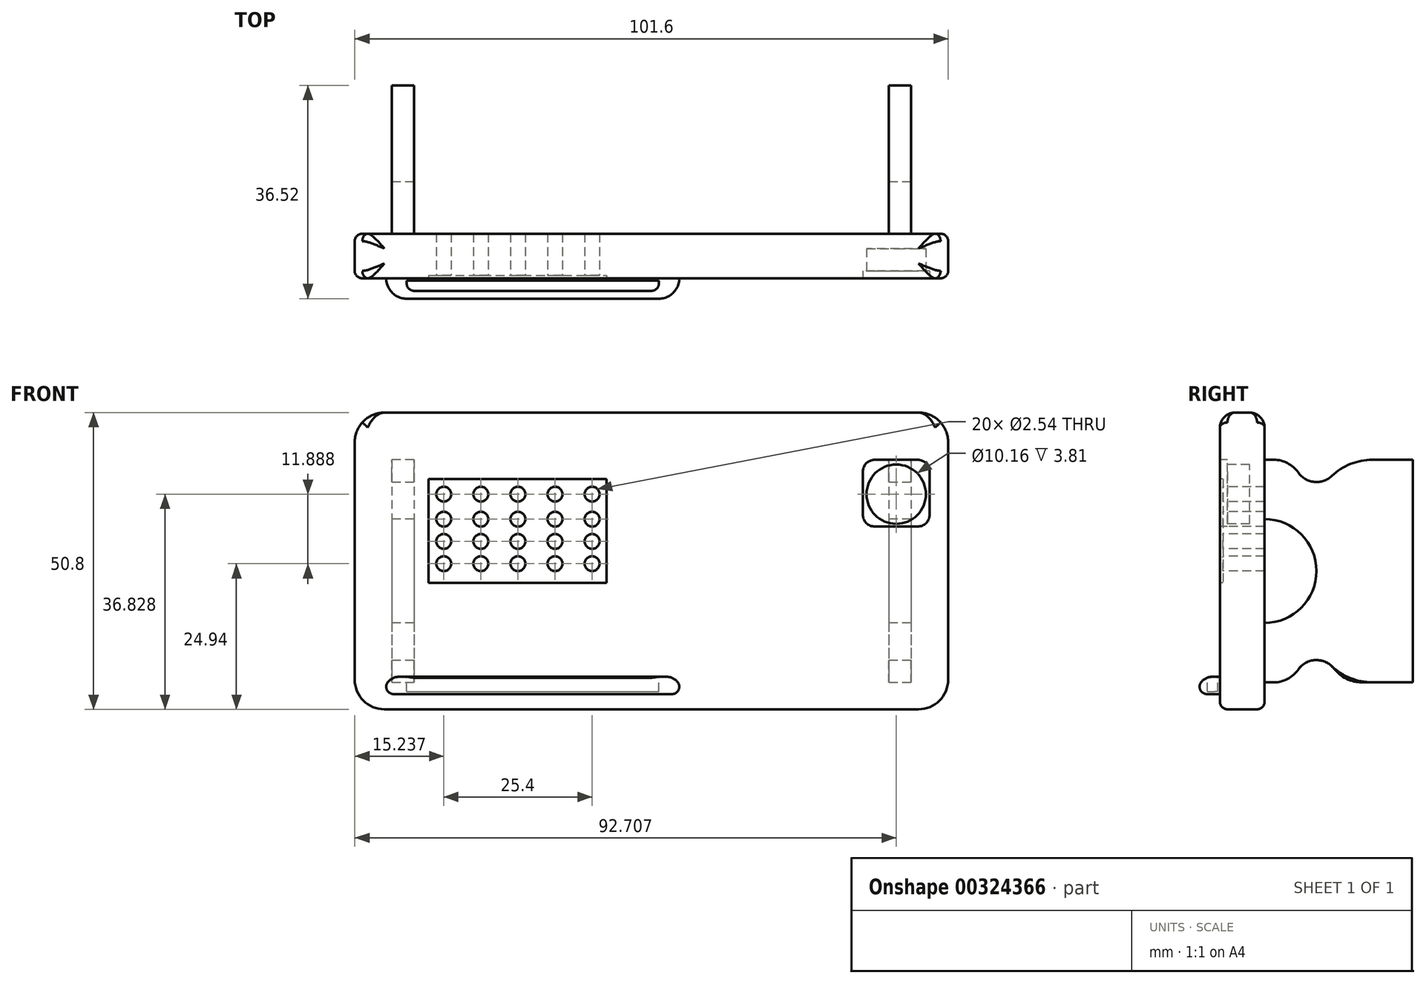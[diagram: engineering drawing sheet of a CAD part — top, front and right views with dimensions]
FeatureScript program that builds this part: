
annotation { "Feature Type Name" : "Feature", "Feature Type Description" : "" }
export const myFeature = defineFeature(function(context is Context, id is Id, definition is map)
    precondition{}
    {
        {
            var Q0;
            Q0=qCreatedBy(makeId("Front.planeOp"),FACE);
            var sketch = newSketch(context, id + "F0", { "sketchPlane" : qUnion([Q0])});
            skLineSegment(sketch, "E0.bottom", {"start": v(-68.61, 8.08) * mm, "end": v(32.99, 8.08) * mm});
            skLineSegment(sketch, "E0.top", {"start": v(-68.61, -42.72) * mm, "end": v(32.99, -42.72) * mm});
            skLineSegment(sketch, "E0.left", {"start": v(-68.61, 8.08) * mm, "end": v(-68.61, -42.72) * mm});
            skLineSegment(sketch, "E0.right", {"start": v(32.99, 8.08) * mm, "end": v(32.99, -42.72) * mm});
            skSolve(sketch);
        }
        {
            var Q0;
            Q0=makeQuery(id+"F0.imprint","IMPRINT",FACE,{"disambiguationData":[TD([[makeQuery(id+"F0.imprint","IMPRINT",EDGE,{"derivedFrom":sQuery(id+"F0.wireOp",EDGE,"E0.bottom")}),-1.0]])]});
            extrude(context, id + "F1", {"entities" : qUnion([Q0]), "depth" : 7.62 * mm});
        }
        {
            var Q0;
            Q0=makeQuery(id+"F1.opExtrude","SWEPT_EDGE",EDGE,{"disambiguationData":[OSD([sQuery(id+"F0.wireOp",EDGE,"E0.bottom"),sQuery(id+"F0.wireOp",EDGE,"E0.left")])]});
            var Q1;
            Q1=makeQuery(id+"F1.opExtrude","SWEPT_EDGE",EDGE,{"disambiguationData":[OSD([sQuery(id+"F0.wireOp",EDGE,"E0.bottom"),sQuery(id+"F0.wireOp",EDGE,"E0.right")])]});
            fillet(context, id + "F2", {"entities" : qUnion([Q0, Q1]), "radius" : 5.08 * mm, "tangentPropagation" : true, "allowEdgeOverflow" : false});
        }
        {
            var Q0;
            Q0=makeQuery(id+"F1.opExtrude","CAP_FACE",FACE,{"disambiguationData":[OSD([sQuery(id+"F0.wireOp",EDGE,"E0.bottom"),sQuery(id+"F0.wireOp",EDGE,"E0.top"),sQuery(id+"F0.wireOp",EDGE,"E0.left"),sQuery(id+"F0.wireOp",EDGE,"E0.right")])],"isStart":false});
            var sketch = newSketch(context, id + "F3", { "sketchPlane" : qUnion([Q0])});
            skLineSegment(sketch, "E1.bottom", {"start": v(-63.53, -37.14) * mm, "end": v(-12.73, -37.14) * mm});
            skLineSegment(sketch, "E1.top", {"start": v(-63.53, -40.12) * mm, "end": v(-12.73, -40.12) * mm});
            skLineSegment(sketch, "E1.left", {"start": v(-63.53, -37.14) * mm, "end": v(-63.53, -40.12) * mm});
            skLineSegment(sketch, "E1.right", {"start": v(-12.73, -37.14) * mm, "end": v(-12.73, -40.12) * mm});
            skSolve(sketch);
        }
        {
            var Q0;
            Q0=makeQuery(id+"F1.opExtrude","SWEPT_EDGE",EDGE,{"disambiguationData":[OSD([sQuery(id+"F0.wireOp",EDGE,"E0.top"),sQuery(id+"F0.wireOp",EDGE,"E0.right")])]});
            var Q1;
            Q1=makeQuery(id+"F1.opExtrude","SWEPT_EDGE",EDGE,{"disambiguationData":[OSD([sQuery(id+"F0.wireOp",EDGE,"E0.top"),sQuery(id+"F0.wireOp",EDGE,"E0.left")])]});
            fillet(context, id + "F4", {"entities" : qUnion([Q0, Q1]), "radius" : 5.08 * mm, "tangentPropagation" : true, "allowEdgeOverflow" : false});
        }
        {
            var Q0;
            Q0=makeQuery(id+"F1.opExtrude","CAP_FACE",FACE,{"disambiguationData":[OSD([sQuery(id+"F0.wireOp",EDGE,"E0.bottom"),sQuery(id+"F0.wireOp",EDGE,"E0.top"),sQuery(id+"F0.wireOp",EDGE,"E0.left"),sQuery(id+"F0.wireOp",EDGE,"E0.right")])],"isStart":false});
            var sketch = newSketch(context, id + "F5", { "sketchPlane" : qUnion([Q0])});
            skLineSegment(sketch, "E2.bottom", {"start": v(19.02, -0.81) * mm, "end": v(29.18, -0.81) * mm});
            skLineSegment(sketch, "E2.top", {"start": v(19.02, -10.97) * mm, "end": v(29.18, -10.97) * mm});
            skLineSegment(sketch, "E2.left", {"start": v(19.02, -0.81) * mm, "end": v(19.02, -10.97) * mm});
            skLineSegment(sketch, "E2.right", {"start": v(29.18, -0.81) * mm, "end": v(29.18, -10.97) * mm});
            skSolve(sketch);
        }
        {
            var Q0;
            Q0=makeQuery(id+"F5.imprint","IMPRINT",FACE,{"disambiguationData":[TD([[makeQuery(id+"F5.imprint","IMPRINT",EDGE,{"derivedFrom":sQuery(id+"F5.wireOp",EDGE,"E2.bottom")}),-1.0]])]});
            extrude(context, id + "F6", {"entities" : qUnion([Q0]), "operationType" : NewBodyOperationType.REMOVE, "oppositeDirection" : true, "depth" : 5.08 * mm});
        }
        {
            var Q0;
            Q0=makeQuery(id+"F6.boolean.opBoolean","COPY",EDGE,{"derivedFrom":makeQuery(id+"F6.opExtrude","SWEPT_EDGE",EDGE,{"disambiguationData":[OSD([sQuery(id+"F5.wireOp",EDGE,"E2.bottom"),sQuery(id+"F5.wireOp",EDGE,"E2.left")])]})});
            var Q1;
            Q1=makeQuery(id+"F6.boolean.opBoolean","COPY",EDGE,{"derivedFrom":makeQuery(id+"F6.opExtrude","SWEPT_EDGE",EDGE,{"disambiguationData":[OSD([sQuery(id+"F5.wireOp",EDGE,"E2.bottom"),sQuery(id+"F5.wireOp",EDGE,"E2.right")])]})});
            var Q2;
            Q2=makeQuery(id+"F6.boolean.opBoolean","COPY",EDGE,{"derivedFrom":makeQuery(id+"F6.opExtrude","SWEPT_EDGE",EDGE,{"disambiguationData":[OSD([sQuery(id+"F5.wireOp",EDGE,"E2.top"),sQuery(id+"F5.wireOp",EDGE,"E2.left")])]})});
            var Q3;
            Q3=makeQuery(id+"F6.boolean.opBoolean","COPY",EDGE,{"derivedFrom":makeQuery(id+"F6.opExtrude","SWEPT_EDGE",EDGE,{"disambiguationData":[OSD([sQuery(id+"F5.wireOp",EDGE,"E2.top"),sQuery(id+"F5.wireOp",EDGE,"E2.right")])]})});
            fillet(context, id + "F7", {"entities" : qUnion([Q0, Q1, Q2, Q3]), "radius" : 5.08 * mm, "tangentPropagation" : true, "allowEdgeOverflow" : false});
        }
        {
            var Q0;
            Q0=makeQuery(id+"F1.opExtrude","CAP_FACE",FACE,{"disambiguationData":[OSD([sQuery(id+"F0.wireOp",EDGE,"E0.bottom"),sQuery(id+"F0.wireOp",EDGE,"E0.top"),sQuery(id+"F0.wireOp",EDGE,"E0.left"),sQuery(id+"F0.wireOp",EDGE,"E0.right")])],"isStart":false});
            var sketch = newSketch(context, id + "F8", { "sketchPlane" : qUnion([Q0])});
            skLineSegment(sketch, "E3.bottom", {"start": v(18.38, 0) * mm, "end": v(29.8, 0) * mm});
            skLineSegment(sketch, "E3.top", {"start": v(18.38, -11.43) * mm, "end": v(29.8, -11.43) * mm});
            skLineSegment(sketch, "E3.left", {"start": v(18.38, 0) * mm, "end": v(18.38, -11.43) * mm});
            skLineSegment(sketch, "E3.right", {"start": v(29.8, 0) * mm, "end": v(29.8, -11.43) * mm});
            skSolve(sketch);
        }
        {
            var Q0;
            Q0=makeQuery(id+"F8.imprint","IMPRINT",FACE,{"disambiguationData":[TD([[makeQuery(id+"F8.imprint","IMPRINT",EDGE,{"derivedFrom":sQuery(id+"F8.wireOp",EDGE,"E3.bottom")}),-1.0]])]});
            extrude(context, id + "F9", {"entities" : qUnion([Q0]), "operationType" : NewBodyOperationType.REMOVE, "oppositeDirection" : true, "depth" : 1.27 * mm});
        }
        {
            var Q0;
            Q0=makeQuery(id+"F9.boolean.opBoolean","COPY",EDGE,{"derivedFrom":makeQuery(id+"F9.opExtrude","SWEPT_EDGE",EDGE,{"disambiguationData":[OSD([sQuery(id+"F8.wireOp",EDGE,"E3.top"),sQuery(id+"F8.wireOp",EDGE,"E3.right")])]})});
            var Q1;
            Q1=makeQuery(id+"F9.boolean.opBoolean","COPY",EDGE,{"derivedFrom":makeQuery(id+"F9.opExtrude","SWEPT_EDGE",EDGE,{"disambiguationData":[OSD([sQuery(id+"F8.wireOp",EDGE,"E3.top"),sQuery(id+"F8.wireOp",EDGE,"E3.left")])]})});
            var Q2;
            Q2=makeQuery(id+"F9.boolean.opBoolean","COPY",EDGE,{"derivedFrom":makeQuery(id+"F9.opExtrude","SWEPT_EDGE",EDGE,{"disambiguationData":[OSD([sQuery(id+"F8.wireOp",EDGE,"E3.bottom"),sQuery(id+"F8.wireOp",EDGE,"E3.left")])]})});
            var Q3;
            Q3=makeQuery(id+"F9.boolean.opBoolean","COPY",EDGE,{"derivedFrom":makeQuery(id+"F9.opExtrude","SWEPT_EDGE",EDGE,{"disambiguationData":[OSD([sQuery(id+"F8.wireOp",EDGE,"E3.bottom"),sQuery(id+"F8.wireOp",EDGE,"E3.right")])]})});
            fillet(context, id + "F10", {"entities" : qUnion([Q0, Q1, Q2, Q3]), "radius" : 2.03 * mm, "tangentPropagation" : true, "allowEdgeOverflow" : false});
        }
        {
            var Q0;
            Q0=makeQuery(id+"F1.opExtrude","SWEPT_FACE",FACE,{"disambiguationData":[OSD([sQuery(id+"F0.wireOp",EDGE,"E0.bottom")])]});
            fillet(context, id + "F11", {"entities" : qUnion([Q0]), "radius" : 2.54 * mm, "allowEdgeOverflow" : false});
        }
        {
            var Q0;
            Q0=makeQuery(id+"F1.opExtrude","CAP_FACE",FACE,{"disambiguationData":[OSD([sQuery(id+"F0.wireOp",EDGE,"E0.bottom"),sQuery(id+"F0.wireOp",EDGE,"E0.top"),sQuery(id+"F0.wireOp",EDGE,"E0.left"),sQuery(id+"F0.wireOp",EDGE,"E0.right")])],"isStart":false});
            var sketch = newSketch(context, id + "F12", { "sketchPlane" : qUnion([Q0])});
            skCircle(sketch, "E4", {"center": v(-53.37, -5.9) * mm, "radius": 1.27 * mm});
            skCircle(sketch, "E5", {"center": v(-53.37, -10.16) * mm, "radius": 1.27 * mm});
            skCircle(sketch, "E6", {"center": v(-53.37, -13.97) * mm, "radius": 1.27 * mm});
            skCircle(sketch, "E7", {"center": v(-53.37, -17.78) * mm, "radius": 1.27 * mm});
            skCircle(sketch, "E8", {"center": v(-47.02, -5.9) * mm, "radius": 1.27 * mm});
            skCircle(sketch, "E9", {"center": v(-47.02, -10.16) * mm, "radius": 1.27 * mm});
            skCircle(sketch, "E10", {"center": v(-47.02, -13.97) * mm, "radius": 1.27 * mm});
            skCircle(sketch, "E11", {"center": v(-47.02, -17.78) * mm, "radius": 1.27 * mm});
            skCircle(sketch, "E12", {"center": v(-40.67, -10.16) * mm, "radius": 1.27 * mm});
            skCircle(sketch, "E13", {"center": v(-40.67, -13.97) * mm, "radius": 1.27 * mm});
            skCircle(sketch, "E14", {"center": v(-40.67, -17.78) * mm, "radius": 1.27 * mm});
            skCircle(sketch, "E15", {"center": v(-40.67, -5.9) * mm, "radius": 1.27 * mm});
            skCircle(sketch, "E16", {"center": v(-34.32, -5.9) * mm, "radius": 1.27 * mm});
            skCircle(sketch, "E17", {"center": v(-34.32, -10.16) * mm, "radius": 1.27 * mm});
            skCircle(sketch, "E18", {"center": v(-34.32, -13.97) * mm, "radius": 1.27 * mm});
            skCircle(sketch, "E19", {"center": v(-34.32, -17.78) * mm, "radius": 1.27 * mm});
            skCircle(sketch, "E20", {"center": v(-27.97, -5.9) * mm, "radius": 1.27 * mm});
            skCircle(sketch, "E21", {"center": v(-27.97, -10.16) * mm, "radius": 1.27 * mm});
            skCircle(sketch, "E22", {"center": v(-27.97, -13.97) * mm, "radius": 1.27 * mm});
            skCircle(sketch, "E23", {"center": v(-27.97, -17.78) * mm, "radius": 1.27 * mm});
            skSolve(sketch);
        }
        {
            var Q0;
            Q0=makeQuery(id+"F12.imprint","IMPRINT",FACE,{"disambiguationData":[TD([[makeQuery(id+"F12.imprint","IMPRINT",EDGE,{"derivedFrom":sQuery(id+"F12.wireOp",EDGE,"E4")}),1.0]])]});
            var Q1;
            Q1=makeQuery(id+"F12.imprint","IMPRINT",FACE,{"disambiguationData":[TD([[makeQuery(id+"F12.imprint","IMPRINT",EDGE,{"derivedFrom":sQuery(id+"F12.wireOp",EDGE,"E5")}),1.0]])]});
            var Q2;
            Q2=makeQuery(id+"F12.imprint","IMPRINT",FACE,{"disambiguationData":[TD([[makeQuery(id+"F12.imprint","IMPRINT",EDGE,{"derivedFrom":sQuery(id+"F12.wireOp",EDGE,"E6")}),1.0]])]});
            var Q3;
            Q3=makeQuery(id+"F12.imprint","IMPRINT",FACE,{"disambiguationData":[TD([[makeQuery(id+"F12.imprint","IMPRINT",EDGE,{"derivedFrom":sQuery(id+"F12.wireOp",EDGE,"E7")}),1.0]])]});
            var Q4;
            Q4=makeQuery(id+"F12.imprint","IMPRINT",FACE,{"disambiguationData":[TD([[makeQuery(id+"F12.imprint","IMPRINT",EDGE,{"derivedFrom":sQuery(id+"F12.wireOp",EDGE,"E11")}),1.0]])]});
            var Q5;
            Q5=makeQuery(id+"F12.imprint","IMPRINT",FACE,{"disambiguationData":[TD([[makeQuery(id+"F12.imprint","IMPRINT",EDGE,{"derivedFrom":sQuery(id+"F12.wireOp",EDGE,"E10")}),1.0]])]});
            var Q6;
            Q6=makeQuery(id+"F12.imprint","IMPRINT",FACE,{"disambiguationData":[TD([[makeQuery(id+"F12.imprint","IMPRINT",EDGE,{"derivedFrom":sQuery(id+"F12.wireOp",EDGE,"E9")}),1.0]])]});
            var Q7;
            Q7=makeQuery(id+"F12.imprint","IMPRINT",FACE,{"disambiguationData":[TD([[makeQuery(id+"F12.imprint","IMPRINT",EDGE,{"derivedFrom":sQuery(id+"F12.wireOp",EDGE,"E8")}),1.0]])]});
            var Q8;
            Q8=makeQuery(id+"F12.imprint","IMPRINT",FACE,{"disambiguationData":[TD([[makeQuery(id+"F12.imprint","IMPRINT",EDGE,{"derivedFrom":sQuery(id+"F12.wireOp",EDGE,"E15")}),1.0]])]});
            var Q9;
            Q9=makeQuery(id+"F12.imprint","IMPRINT",FACE,{"disambiguationData":[TD([[makeQuery(id+"F12.imprint","IMPRINT",EDGE,{"derivedFrom":sQuery(id+"F12.wireOp",EDGE,"E16")}),1.0]])]});
            var Q10;
            Q10=makeQuery(id+"F12.imprint","IMPRINT",FACE,{"disambiguationData":[TD([[makeQuery(id+"F12.imprint","IMPRINT",EDGE,{"derivedFrom":sQuery(id+"F12.wireOp",EDGE,"E20")}),1.0]])]});
            var Q11;
            Q11=makeQuery(id+"F12.imprint","IMPRINT",FACE,{"disambiguationData":[TD([[makeQuery(id+"F12.imprint","IMPRINT",EDGE,{"derivedFrom":sQuery(id+"F12.wireOp",EDGE,"E12")}),1.0]])]});
            var Q12;
            Q12=makeQuery(id+"F12.imprint","IMPRINT",FACE,{"disambiguationData":[TD([[makeQuery(id+"F12.imprint","IMPRINT",EDGE,{"derivedFrom":sQuery(id+"F12.wireOp",EDGE,"E13")}),1.0]])]});
            var Q13;
            Q13=makeQuery(id+"F12.imprint","IMPRINT",FACE,{"disambiguationData":[TD([[makeQuery(id+"F12.imprint","IMPRINT",EDGE,{"derivedFrom":sQuery(id+"F12.wireOp",EDGE,"E14")}),1.0]])]});
            var Q14;
            Q14=makeQuery(id+"F12.imprint","IMPRINT",FACE,{"disambiguationData":[TD([[makeQuery(id+"F12.imprint","IMPRINT",EDGE,{"derivedFrom":sQuery(id+"F12.wireOp",EDGE,"E19")}),1.0]])]});
            var Q15;
            Q15=makeQuery(id+"F12.imprint","IMPRINT",FACE,{"disambiguationData":[TD([[makeQuery(id+"F12.imprint","IMPRINT",EDGE,{"derivedFrom":sQuery(id+"F12.wireOp",EDGE,"E18")}),1.0]])]});
            var Q16;
            Q16=makeQuery(id+"F12.imprint","IMPRINT",FACE,{"disambiguationData":[TD([[makeQuery(id+"F12.imprint","IMPRINT",EDGE,{"derivedFrom":sQuery(id+"F12.wireOp",EDGE,"E17")}),1.0]])]});
            var Q17;
            Q17=makeQuery(id+"F12.imprint","IMPRINT",FACE,{"disambiguationData":[TD([[makeQuery(id+"F12.imprint","IMPRINT",EDGE,{"derivedFrom":sQuery(id+"F12.wireOp",EDGE,"E21")}),1.0]])]});
            var Q18;
            Q18=makeQuery(id+"F12.imprint","IMPRINT",FACE,{"disambiguationData":[TD([[makeQuery(id+"F12.imprint","IMPRINT",EDGE,{"derivedFrom":sQuery(id+"F12.wireOp",EDGE,"E22")}),1.0]])]});
            var Q19;
            Q19=makeQuery(id+"F12.imprint","IMPRINT",FACE,{"disambiguationData":[TD([[makeQuery(id+"F12.imprint","IMPRINT",EDGE,{"derivedFrom":sQuery(id+"F12.wireOp",EDGE,"E23")}),1.0]])]});
            extrude(context, id + "F13", {"entities" : qUnion([Q0, Q1, Q2, Q3, Q4, Q5, Q6, Q7, Q8, Q9, Q10, Q11, Q12, Q13, Q14, Q15, Q16, Q17, Q18, Q19]), "operationType" : NewBodyOperationType.REMOVE, "oppositeDirection" : true, "depth" : 25.4 * mm});
        }
        {
            var Q0;
            Q0=makeQuery(id+"F1.opExtrude","CAP_FACE",FACE,{"disambiguationData":[OSD([sQuery(id+"F0.wireOp",EDGE,"E0.bottom"),sQuery(id+"F0.wireOp",EDGE,"E0.top"),sQuery(id+"F0.wireOp",EDGE,"E0.left"),sQuery(id+"F0.wireOp",EDGE,"E0.right")])],"isStart":false});
            var sketch = newSketch(context, id + "F14", { "sketchPlane" : qUnion([Q0])});
            skLineSegment(sketch, "E24.bottom", {"start": v(-55.97, -3.3) * mm, "end": v(-25.5, -3.3) * mm});
            skLineSegment(sketch, "E24.top", {"start": v(-55.97, -21.08) * mm, "end": v(-25.5, -21.08) * mm});
            skLineSegment(sketch, "E24.left", {"start": v(-55.97, -3.3) * mm, "end": v(-55.97, -21.08) * mm});
            skLineSegment(sketch, "E24.right", {"start": v(-25.5, -3.3) * mm, "end": v(-25.5, -21.08) * mm});
            skSolve(sketch);
        }
        {
            var Q0;
            Q0=makeQuery(id+"F14.imprint","IMPRINT",FACE,{"disambiguationData":[TD([[makeQuery(id+"F14.imprint","IMPRINT",EDGE,{"derivedFrom":sQuery(id+"F14.wireOp",EDGE,"E24.bottom")}),-1.0]])]});
            extrude(context, id + "F15", {"entities" : qUnion([Q0]), "operationType" : NewBodyOperationType.REMOVE, "oppositeDirection" : true, "depth" : 0.5 * mm});
        }
        {
            var Q0;
            Q0=makeQuery(id+"F1.opExtrude","CAP_FACE",FACE,{"disambiguationData":[OSD([sQuery(id+"F0.wireOp",EDGE,"E0.bottom"),sQuery(id+"F0.wireOp",EDGE,"E0.top"),sQuery(id+"F0.wireOp",EDGE,"E0.left"),sQuery(id+"F0.wireOp",EDGE,"E0.right")])],"isStart":true});
            var sketch = newSketch(context, id + "F16", { "sketchPlane" : qUnion([Q0])});
            skLineSegment(sketch, "E25.bottom", {"start": v(-26.64, 0) * mm, "end": v(-22.83, 0) * mm});
            skLineSegment(sketch, "E25.top", {"start": v(-26.64, -38.1) * mm, "end": v(-22.83, -38.1) * mm});
            skLineSegment(sketch, "E25.left", {"start": v(-26.64, 0) * mm, "end": v(-26.64, -38.1) * mm});
            skLineSegment(sketch, "E25.right", {"start": v(-22.83, 0) * mm, "end": v(-22.83, -38.1) * mm});
            skLineSegment(sketch, "E26.bottom", {"start": v(58.45, 0) * mm, "end": v(62.26, 0) * mm});
            skLineSegment(sketch, "E26.top", {"start": v(58.45, -38.1) * mm, "end": v(62.26, -38.1) * mm});
            skLineSegment(sketch, "E26.left", {"start": v(58.45, 0) * mm, "end": v(58.45, -38.1) * mm});
            skLineSegment(sketch, "E26.right", {"start": v(62.26, 0) * mm, "end": v(62.26, -38.1) * mm});
            skSolve(sketch);
        }
        {
            var Q0;
            Q0=makeQuery(id+"F16.imprint","IMPRINT",FACE,{"disambiguationData":[TD([[makeQuery(id+"F16.imprint","IMPRINT",EDGE,{"derivedFrom":sQuery(id+"F16.wireOp",EDGE,"E25.bottom")}),-1.0]])]});
            var Q1;
            Q1=makeQuery(id+"F16.imprint","IMPRINT",FACE,{"disambiguationData":[TD([[makeQuery(id+"F16.imprint","IMPRINT",EDGE,{"derivedFrom":sQuery(id+"F16.wireOp",EDGE,"E26.bottom")}),-1.0]])]});
            extrude(context, id + "F17", {"entities" : qUnion([Q0, Q1]), "operationType" : NewBodyOperationType.ADD, "depth" : 25.4 * mm});
        }
        {
            var Q0;
            Q0=makeQuery(id+"F17.opExtrude","SWEPT_FACE",FACE,{"disambiguationData":[OSD([sQuery(id+"F16.wireOp",EDGE,"E25.left")])]});
            var sketch = newSketch(context, id + "F18", { "sketchPlane" : qUnion([Q0])});
            skCircle(sketch, "E27", {"center": v(8.9, -38.1) * mm, "radius": 3.81 * mm});
            skCircle(sketch, "E28", {"center": v(8.89, 0) * mm, "radius": 3.81 * mm});
            skSolve(sketch);
        }
        {
            var Q0;
            {var subQ0=sQuery(id+"F18.wireOp",EDGE,"E27");var subQ1=makeQuery(id+"F17.opExtrude","SWEPT_EDGE",EDGE,{"disambiguationData":[OSD([sQuery(id+"F16.wireOp",EDGE,"E25.top"),sQuery(id+"F16.wireOp",EDGE,"E25.left")])]});var subQ2=makeQuery(id+"F18.imprint","INTERSECT",VERTEX,{"disambiguationData":[OD(0.0)],"derivedFrom":[subQ1,subQ0]});Q0=makeQuery(id+"F18.imprint","IMPRINT",FACE,{"disambiguationData":[TD([[makeQuery(id+"F18.imprint","IMPRINT",EDGE,{"disambiguationData":[TD([[subQ2,-1.0]])],"derivedFrom":subQ0}),1.0]])]});}
            var Q1;
            {var subQ0=sQuery(id+"F18.wireOp",EDGE,"E28");var subQ1=makeQuery(id+"F17.opExtrude","SWEPT_EDGE",EDGE,{"disambiguationData":[OSD([sQuery(id+"F16.wireOp",EDGE,"E25.bottom"),sQuery(id+"F16.wireOp",EDGE,"E25.left")])]});var subQ2=makeQuery(id+"F18.imprint","INTERSECT",VERTEX,{"disambiguationData":[OD(0.0)],"derivedFrom":[subQ1,subQ0]});Q1=makeQuery(id+"F18.imprint","IMPRINT",FACE,{"disambiguationData":[TD([[makeQuery(id+"F18.imprint","IMPRINT",EDGE,{"disambiguationData":[TD([[subQ2,-1.0]])],"derivedFrom":subQ0}),1.0]])]});}
            var Q2;
            {var subQ0=sQuery(id+"F18.wireOp",EDGE,"E28");var subQ1=makeQuery(id+"F17.opExtrude","SWEPT_EDGE",EDGE,{"disambiguationData":[OSD([sQuery(id+"F16.wireOp",EDGE,"E25.bottom"),sQuery(id+"F16.wireOp",EDGE,"E25.left")])]});var subQ2=makeQuery(id+"F18.imprint","INTERSECT",VERTEX,{"disambiguationData":[OD(0.0)],"derivedFrom":[subQ1,subQ0]});Q2=makeQuery(id+"F18.imprint","IMPRINT",FACE,{"disambiguationData":[TD([[makeQuery(id+"F18.imprint","IMPRINT",EDGE,{"disambiguationData":[TD([[subQ2,1.0]])],"derivedFrom":subQ0}),1.0]])]});}
            var Q3;
            {var subQ0=sQuery(id+"F18.wireOp",EDGE,"E27");var subQ1=makeQuery(id+"F17.opExtrude","SWEPT_EDGE",EDGE,{"disambiguationData":[OSD([sQuery(id+"F16.wireOp",EDGE,"E25.top"),sQuery(id+"F16.wireOp",EDGE,"E25.left")])]});var subQ2=makeQuery(id+"F18.imprint","INTERSECT",VERTEX,{"disambiguationData":[OD(0.0)],"derivedFrom":[subQ1,subQ0]});Q3=makeQuery(id+"F18.imprint","IMPRINT",FACE,{"disambiguationData":[TD([[makeQuery(id+"F18.imprint","IMPRINT",EDGE,{"disambiguationData":[TD([[subQ2,1.0]])],"derivedFrom":subQ0}),1.0]])]});}
            extrude(context, id + "F19", {"entities" : qUnion([Q0, Q1, Q2, Q3]), "operationType" : NewBodyOperationType.REMOVE, "oppositeDirection" : true, "depth" : 203.2 * mm});
        }
        {
            var Q0;
            Q0=makeQuery(id+"F19.boolean.opBoolean","INTERSECT",EDGE,{"disambiguationData":[OD(0.0)],"derivedFrom":[makeQuery(id+"F17.opExtrude","SWEPT_FACE",FACE,{"disambiguationData":[OSD([sQuery(id+"F16.wireOp",EDGE,"E25.top")])]}),makeQuery(id+"F19.opExtrude","SWEPT_FACE",FACE,{"disambiguationData":[OSD([sQuery(id+"F18.wireOp",EDGE,"E27")])]})]});
            var Q1;
            Q1=makeQuery(id+"F19.boolean.opBoolean","INTERSECT",EDGE,{"disambiguationData":[OD(0.0)],"derivedFrom":[makeQuery(id+"F17.opExtrude","SWEPT_FACE",FACE,{"disambiguationData":[OSD([sQuery(id+"F16.wireOp",EDGE,"E25.bottom")])]}),makeQuery(id+"F19.opExtrude","SWEPT_FACE",FACE,{"disambiguationData":[OSD([sQuery(id+"F18.wireOp",EDGE,"E28")])]})]});
            var Q2;
            Q2=makeQuery(id+"F19.boolean.opBoolean","INTERSECT",EDGE,{"disambiguationData":[OD(0.0)],"derivedFrom":[makeQuery(id+"F17.opExtrude","SWEPT_FACE",FACE,{"disambiguationData":[OSD([sQuery(id+"F16.wireOp",EDGE,"E26.bottom")])]}),makeQuery(id+"F19.opExtrude","SWEPT_FACE",FACE,{"disambiguationData":[OSD([sQuery(id+"F18.wireOp",EDGE,"E28")])]})]});
            fillet(context, id + "F20", {"entities" : qUnion([Q0, Q1, Q2]), "radius" : 10.16 * mm, "tangentPropagation" : true, "allowEdgeOverflow" : false});
        }
        {
            var Q0;
            Q0=makeQuery(id+"F19.boolean.opBoolean","INTERSECT",EDGE,{"disambiguationData":[OD(1.0)],"derivedFrom":[makeQuery(id+"F17.opExtrude","SWEPT_FACE",FACE,{"disambiguationData":[OSD([sQuery(id+"F16.wireOp",EDGE,"E26.top")])]}),makeQuery(id+"F19.opExtrude","SWEPT_FACE",FACE,{"disambiguationData":[OSD([sQuery(id+"F18.wireOp",EDGE,"E27")])]})]});
            var Q1;
            Q1=makeQuery(id+"F19.boolean.opBoolean","INTERSECT",EDGE,{"disambiguationData":[OD(1.0)],"derivedFrom":[makeQuery(id+"F17.opExtrude","SWEPT_FACE",FACE,{"disambiguationData":[OSD([sQuery(id+"F16.wireOp",EDGE,"E25.top")])]}),makeQuery(id+"F19.opExtrude","SWEPT_FACE",FACE,{"disambiguationData":[OSD([sQuery(id+"F18.wireOp",EDGE,"E27")])]})]});
            var Q2;
            Q2=makeQuery(id+"F19.boolean.opBoolean","INTERSECT",EDGE,{"disambiguationData":[OD(1.0)],"derivedFrom":[makeQuery(id+"F17.opExtrude","SWEPT_FACE",FACE,{"disambiguationData":[OSD([sQuery(id+"F16.wireOp",EDGE,"E25.bottom")])]}),makeQuery(id+"F19.opExtrude","SWEPT_FACE",FACE,{"disambiguationData":[OSD([sQuery(id+"F18.wireOp",EDGE,"E28")])]})]});
            var Q3;
            Q3=makeQuery(id+"F19.boolean.opBoolean","INTERSECT",EDGE,{"disambiguationData":[OD(1.0)],"derivedFrom":[makeQuery(id+"F17.opExtrude","SWEPT_FACE",FACE,{"disambiguationData":[OSD([sQuery(id+"F16.wireOp",EDGE,"E26.bottom")])]}),makeQuery(id+"F19.opExtrude","SWEPT_FACE",FACE,{"disambiguationData":[OSD([sQuery(id+"F18.wireOp",EDGE,"E28")])]})]});
            fillet(context, id + "F21", {"entities" : qUnion([Q0, Q1, Q2, Q3]), "radius" : 5.08 * mm, "tangentPropagation" : true, "allowEdgeOverflow" : false});
        }
        {
            var Q0;
            Q0=makeQuery(id+"F19.boolean.opBoolean","INTERSECT",EDGE,{"disambiguationData":[OD(0.0)],"derivedFrom":[makeQuery(id+"F17.opExtrude","SWEPT_FACE",FACE,{"disambiguationData":[OSD([sQuery(id+"F16.wireOp",EDGE,"E26.top")])]}),makeQuery(id+"F19.opExtrude","SWEPT_FACE",FACE,{"disambiguationData":[OSD([sQuery(id+"F18.wireOp",EDGE,"E27")])]})]});
            fillet(context, id + "F22", {"entities" : qUnion([Q0]), "radius" : 6.1 * mm, "tangentPropagation" : true, "allowEdgeOverflow" : false});
        }
        {
            var Q0;
            Q0=makeQuery(id+"F3.imprint","IMPRINT",FACE,{"disambiguationData":[TD([[makeQuery(id+"F3.imprint","IMPRINT",EDGE,{"derivedFrom":sQuery(id+"F3.wireOp",EDGE,"E1.bottom")}),-1.0]])]});
            extrude(context, id + "F23", {"entities" : qUnion([Q0]), "operationType" : NewBodyOperationType.ADD, "depth" : 3.8 * mm});
        }
        {
            var Q0;
            Q0=makeQuery(id+"F23.opExtrude","CAP_EDGE",EDGE,{"disambiguationData":[OSD([sQuery(id+"F3.wireOp",EDGE,"E1.left")])],"isStart":false});
            var Q1;
            Q1=makeQuery(id+"F23.opExtrude","CAP_EDGE",EDGE,{"disambiguationData":[OSD([sQuery(id+"F3.wireOp",EDGE,"E1.right")])],"isStart":false});
            fillet(context, id + "F24", {"entities" : qUnion([Q0, Q1]), "radius" : 3.8 * mm, "tangentPropagation" : true, "allowEdgeOverflow" : false});
        }
        {
            var Q0;
            Q0=makeQuery(id+"F23.opExtrude","SWEPT_FACE",FACE,{"disambiguationData":[OSD([sQuery(id+"F3.wireOp",EDGE,"E1.bottom")])]});
            var sketch = newSketch(context, id + "F25", { "sketchPlane" : qUnion([Q0])});
            skLineSegment(sketch, "E29.bottom", {"start": v(-59.72, -8) * mm, "end": v(-16.54, -8) * mm});
            skLineSegment(sketch, "E29.top", {"start": v(-59.72, -9.78) * mm, "end": v(-16.54, -9.78) * mm});
            skLineSegment(sketch, "E29.left", {"start": v(-59.72, -8) * mm, "end": v(-59.72, -9.78) * mm});
            skLineSegment(sketch, "E29.right", {"start": v(-16.54, -8) * mm, "end": v(-16.54, -9.78) * mm});
            skSolve(sketch);
        }
        {
            var Q0;
            Q0=makeQuery(id+"F25.imprint","IMPRINT",FACE,{"disambiguationData":[TD([[makeQuery(id+"F25.imprint","IMPRINT",EDGE,{"derivedFrom":sQuery(id+"F25.wireOp",EDGE,"E29.bottom")}),-1.0]])]});
            extrude(context, id + "F26", {"entities" : qUnion([Q0]), "operationType" : NewBodyOperationType.REMOVE, "oppositeDirection" : true, "depth" : 2.54 * mm});
        }
        {
            var Q0;
            Q0=makeQuery(id+"F24.opFillet","BLEND_EDGE",EDGE,{"blendedFrom":[makeQuery(id+"F23.opExtrude","CAP_EDGE",EDGE,{"disambiguationData":[OSD([sQuery(id+"F3.wireOp",EDGE,"E1.left")])],"isStart":false}),makeQuery(id+"F23.opExtrude","SWEPT_FACE",FACE,{"disambiguationData":[OSD([sQuery(id+"F3.wireOp",EDGE,"E1.bottom")])]})],"blendedInto":[makeQuery(id+"F23.opExtrude","SWEPT_FACE",FACE,{"disambiguationData":[OSD([sQuery(id+"F3.wireOp",EDGE,"E1.bottom")])]})]});
            fillet(context, id + "F27", {"entities" : qUnion([Q0]), "radius" : 2.54 * mm, "tangentPropagation" : true, "allowEdgeOverflow" : false});
        }
        {
            var Q0;
            Q0=makeQuery(id+"F26.boolean.opBoolean","COPY",EDGE,{"derivedFrom":makeQuery(id+"F26.opExtrude","SWEPT_EDGE",EDGE,{"disambiguationData":[OSD([sQuery(id+"F25.wireOp",EDGE,"E29.top"),sQuery(id+"F25.wireOp",EDGE,"E29.left")])]})});
            var Q1;
            Q1=makeQuery(id+"F26.boolean.opBoolean","COPY",EDGE,{"derivedFrom":makeQuery(id+"F26.opExtrude","SWEPT_EDGE",EDGE,{"disambiguationData":[OSD([sQuery(id+"F25.wireOp",EDGE,"E29.top"),sQuery(id+"F25.wireOp",EDGE,"E29.right")])]})});
            fillet(context, id + "F28", {"entities" : qUnion([Q0, Q1]), "radius" : 1.27 * mm, "tangentPropagation" : true, "allowEdgeOverflow" : false});
        }
        {
            var Q0;
            Q0=makeQuery(id+"F23.opExtrude","CAP_EDGE",EDGE,{"disambiguationData":[OSD([sQuery(id+"F3.wireOp",EDGE,"E1.top")])],"isStart":false});
            fillet(context, id + "F29", {"entities" : qUnion([Q0]), "radius" : 2.54 * mm, "tangentPropagation" : true, "allowEdgeOverflow" : false});
        }
        {
            var Q0;
            Q0=makeQuery(id+"F29.opFillet","BLEND_EDGE",EDGE,{"blendedFrom":[makeQuery(id+"F23.opExtrude","CAP_EDGE",EDGE,{"disambiguationData":[OSD([sQuery(id+"F3.wireOp",EDGE,"E1.top")])],"isStart":false}),makeQuery(id+"F27.opFillet","BLEND_FACE",FACE,{"disambiguationData":[OSD([sQuery(id+"F3.wireOp",EDGE,"E1.bottom")])]})],"blendedInto":[makeQuery(id+"F27.opFillet","BLEND_FACE",FACE,{"disambiguationData":[OSD([sQuery(id+"F3.wireOp",EDGE,"E1.bottom")])]})]});
            fillet(context, id + "F30", {"entities" : qUnion([Q0]), "radius" : 1.27 * mm, "tangentPropagation" : true, "allowEdgeOverflow" : false});
        }
        {
            var Q0;
            Q0=makeQuery(id+"F1.opExtrude","CAP_EDGE",EDGE,{"disambiguationData":[OSD([sQuery(id+"F0.wireOp",EDGE,"E0.left")])],"isStart":true});
            var Q1;
            Q1=makeQuery(id+"F1.opExtrude","CAP_EDGE",EDGE,{"disambiguationData":[OSD([sQuery(id+"F0.wireOp",EDGE,"E0.left")])],"isStart":false});
            fillet(context, id + "F31", {"entities" : qUnion([Q0, Q1]), "radius" : 1.27 * mm, "tangentPropagation" : true, "allowEdgeOverflow" : false});
        }
        {
            var Q0;
            Q0=makeQuery(id+"F17.opExtrude","SWEPT_FACE",FACE,{"disambiguationData":[OSD([sQuery(id+"F16.wireOp",EDGE,"E26.right")])]});
            var sketch = newSketch(context, id + "F32", { "sketchPlane" : qUnion([Q0])});
            skArc(sketch, "E30", {"start": v(0, -10.16) * mm, "mid": v(-8.9, -19.05) * mm, "end": v(0, -27.94) * mm});
            skLineSegment(sketch, "E31", {"start": v(0, -10.16) * mm, "end": v(0, -27.94) * mm});
            skPoint(sketch, "E32.orphan", {"position": v(0, 10.87) * mm});
            skSolve(sketch);
        }
        {
            var Q0;
            Q0=makeQuery(id+"F32.imprint","IMPRINT",FACE,{"disambiguationData":[TD([[makeQuery(id+"F32.imprint","IMPRINT",EDGE,{"derivedFrom":sQuery(id+"F32.wireOp",EDGE,"E30")}),1.0]])]});
            extrude(context, id + "F33", {"entities" : qUnion([Q0]), "operationType" : NewBodyOperationType.REMOVE, "oppositeDirection" : true, "depth" : 254 * mm});
        }
    });
